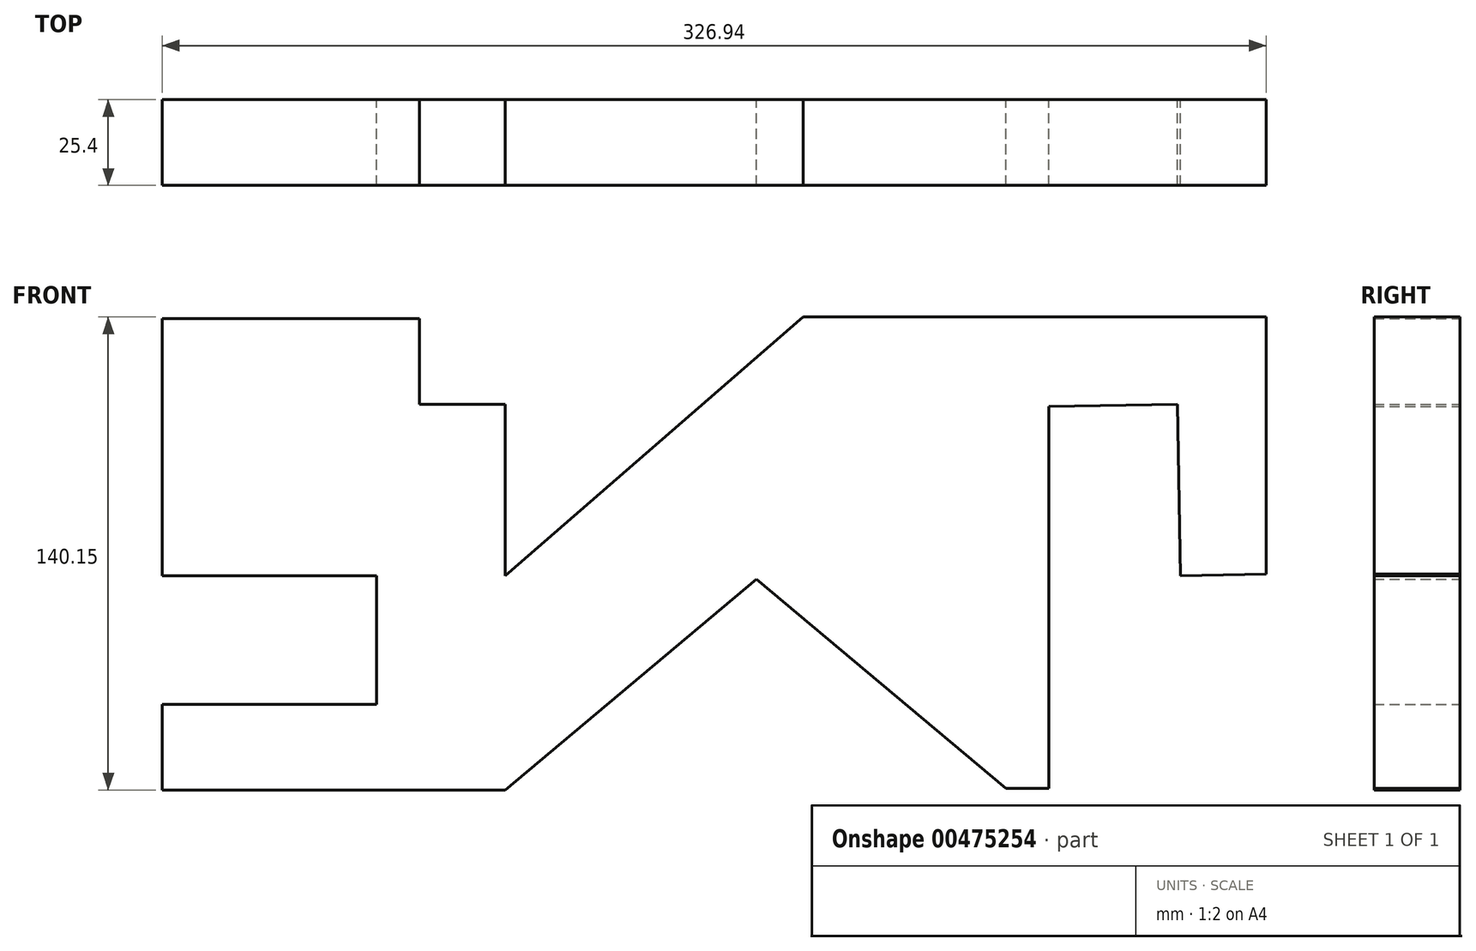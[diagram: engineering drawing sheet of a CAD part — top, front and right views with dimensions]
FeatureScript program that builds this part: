
annotation { "Feature Type Name" : "Feature", "Feature Type Description" : "" }
export const myFeature = defineFeature(function(context is Context, id is Id, definition is map)
    precondition{}
    {
        {
            var Q0;
            Q0=qCreatedBy(makeId("Front.planeOp"),FACE);
            var sketch = newSketch(context, id + "F0", { "sketchPlane" : qUnion([Q0])});
            skLineSegment(sketch, "E0", {"start": v(0, -63.5) * mm, "end": v(-101.6, -63.5) * mm});
            skLineSegment(sketch, "E1", {"start": v(-101.6, -63.5) * mm, "end": v(-101.6, -38.1) * mm});
            skLineSegment(sketch, "E2", {"start": v(-101.6, -38.1) * mm, "end": v(-38.1, -38.1) * mm});
            skLineSegment(sketch, "E3", {"start": v(-38.1, -38.1) * mm, "end": v(-38.1, 0) * mm});
            skLineSegment(sketch, "E4", {"start": v(-38.1, 0) * mm, "end": v(-101.6, 0) * mm});
            skLineSegment(sketch, "E5", {"start": v(-101.6, 0) * mm, "end": v(-101.6, 76.2) * mm});
            skLineSegment(sketch, "E6", {"start": v(-101.6, 76.2) * mm, "end": v(-25.4, 76.2) * mm});
            skLineSegment(sketch, "E7", {"start": v(-25.4, 76.2) * mm, "end": v(-25.4, 50.8) * mm});
            skLineSegment(sketch, "E8", {"start": v(-25.4, 50.8) * mm, "end": v(0, 50.8) * mm});
            skLineSegment(sketch, "E9", {"start": v(0, 50.8) * mm, "end": v(0, 0) * mm});
            skLineSegment(sketch, "E10", {"start": v(0, 0) * mm, "end": v(88.18, 76.65) * mm});
            skLineSegment(sketch, "E11", {"start": v(88.18, 76.65) * mm, "end": v(225.34, 76.65) * mm});
            skLineSegment(sketch, "E12", {"start": v(225.34, 76.65) * mm, "end": v(225.34, 0.45) * mm});
            skLineSegment(sketch, "E13", {"start": v(225.34, 0.45) * mm, "end": v(199.94, 0) * mm});
            skLineSegment(sketch, "E14", {"start": v(199.94, 0) * mm, "end": v(199.04, 50.8) * mm});
            skLineSegment(sketch, "E15", {"start": v(199.04, 50.8) * mm, "end": v(160.94, 50.11) * mm});
            skLineSegment(sketch, "E16", {"start": v(160.94, 50.11) * mm, "end": v(160.94, -63.05) * mm});
            skLineSegment(sketch, "E17", {"start": v(160.94, -63.05) * mm, "end": v(148.24, -63.05) * mm});
            skLineSegment(sketch, "E18", {"start": v(148.24, -63.05) * mm, "end": v(74.4, -1.08) * mm});
            skLineSegment(sketch, "E19", {"start": v(74.4, -1.08) * mm, "end": v(0, -63.5) * mm});
            skLineSegment(sketch, "E20", {"start": v(0, -63.5) * mm, "end": v(26.07, -63.5) * mm});
            skSolve(sketch);
        }
        {
            var Q0;
            Q0=makeQuery(id+"F0.imprint","IMPRINT",FACE,{"disambiguationData":[TD([[makeQuery(id+"F0.imprint","IMPRINT",EDGE,{"derivedFrom":sQuery(id+"F0.wireOp",EDGE,"E0")}),-1.0]])]});
            extrude(context, id + "F1", {"entities" : qUnion([Q0]), "depth" : 25.4 * mm});
        }
    });
